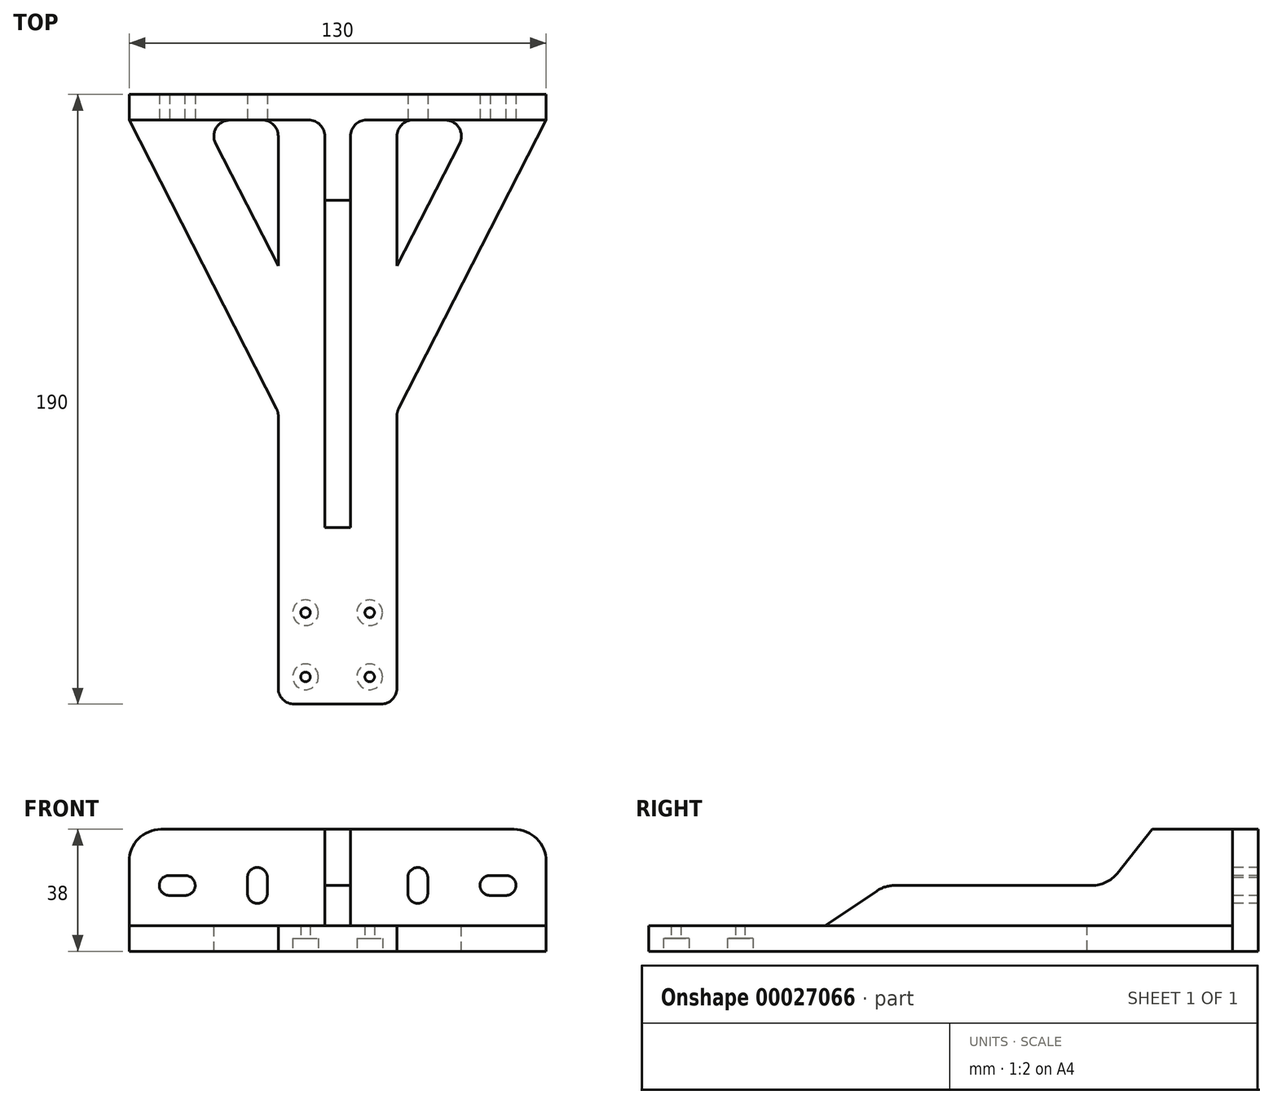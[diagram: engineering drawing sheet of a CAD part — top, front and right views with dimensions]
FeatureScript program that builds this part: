
annotation { "Feature Type Name" : "Feature", "Feature Type Description" : "" }
export const myFeature = defineFeature(function(context is Context, id is Id, definition is map)
    precondition{}
    {
        {
            var Q0;
            Q0=qCreatedBy(makeId("Top.planeOp"),FACE);
            var sketch = newSketch(context, id + "F0", { "sketchPlane" : qUnion([Q0])});
            skLineSegment(sketch, "E0", {"start": v(21.29, 30.4) * mm, "end": v(21.29, -54.4) * mm});
            skLineSegment(sketch, "E1", {"start": v(16.29, -59.4) * mm, "end": v(-10.71, -59.4) * mm});
            skLineSegment(sketch, "E2", {"start": v(-15.71, -54.4) * mm, "end": v(-15.71, 30.4) * mm});
            skLineSegment(sketch, "E3", {"start": v(-62.21, 130.6) * mm, "end": v(67.79, 130.6) * mm});
            skLineSegment(sketch, "E4", {"start": v(67.79, 130.6) * mm, "end": v(67.79, 122.6) * mm});
            skLineSegment(sketch, "E5", {"start": v(-62.21, 122.6) * mm, "end": v(-62.21, 130.6) * mm});
            skLineSegment(sketch, "E6", {"start": v(-16.26, 32.67) * mm, "end": v(-62.21, 122.6) * mm});
            skLineSegment(sketch, "E7", {"start": v(21.83, 32.67) * mm, "end": v(67.79, 122.6) * mm});
            skPoint(sketch, "E8.end.orphan", {"position": v(21.29, 122.6) * mm});
            skPoint(sketch, "E9.orphan", {"position": v(-15.71, 122.6) * mm});
            skPoint(sketch, "E10.visualSharp", {"position": v(-15.71, -59.4) * mm});
            skArc(sketch, "E10.filletArc", {"start": v(-15.71, -54.4) * mm, "mid": v(-14.25, -57.93) * mm, "end": v(-10.71, -59.4) * mm});
            skPoint(sketch, "E11.visualSharp", {"position": v(21.29, -59.4) * mm});
            skArc(sketch, "E11.filletArc", {"start": v(16.29, -59.4) * mm, "mid": v(19.82, -57.93) * mm, "end": v(21.29, -54.4) * mm});
            skPoint(sketch, "E12.visualSharp", {"position": v(21.29, 31.6) * mm});
            skArc(sketch, "E12.filletArc", {"start": v(21.83, 32.67) * mm, "mid": v(21.42, 31.57) * mm, "end": v(21.29, 30.4) * mm});
            skPoint(sketch, "E13.visualSharp", {"position": v(-15.71, 31.6) * mm});
            skArc(sketch, "E13.filletArc", {"start": v(-15.71, 30.4) * mm, "mid": v(-15.85, 31.57) * mm, "end": v(-16.26, 32.67) * mm});
            skLineSegment(sketch, "E14", {"start": v(-15.71, 122.6) * mm, "end": v(-38.96, 122.6) * mm});
            skLineSegment(sketch, "E15", {"start": v(-15.71, 122.6) * mm, "end": v(-15.71, 77.1) * mm});
            skLineSegment(sketch, "E16", {"start": v(-38.96, 122.6) * mm, "end": v(-15.71, 77.1) * mm});
            skLineSegment(sketch, "E17.MirrorCS", {"start": v(21.29, 122.6) * mm, "end": v(21.29, 77.1) * mm});
            skLineSegment(sketch, "E18.MirrorCS", {"start": v(44.54, 122.6) * mm, "end": v(21.29, 77.1) * mm});
            skLineSegment(sketch, "E19.MirrorCS", {"start": v(21.29, 122.6) * mm, "end": v(44.54, 122.6) * mm});
            skSolve(sketch);
        }
        {
            var Q0;
            Q0=makeQuery(id+"F0.imprint","IMPRINT",FACE,{"disambiguationData":[TD([[makeQuery(id+"F0.imprint","IMPRINT",EDGE,{"derivedFrom":sQuery(id+"F0.wireOp",EDGE,"E0")}),-1.0]])]});
            extrude(context, id + "F1", {"entities" : qUnion([Q0]), "depth" : 8 * mm});
        }
        {
            var Q0;
            Q0=makeQuery(id+"F1.opExtrude","CAP_FACE",FACE,{"disambiguationData":[OSD([sQuery(id+"F0.wireOp",EDGE,"E0"),sQuery(id+"F0.wireOp",EDGE,"E1"),sQuery(id+"F0.wireOp",EDGE,"E2"),sQuery(id+"F0.wireOp",EDGE,"E3"),sQuery(id+"F0.wireOp",EDGE,"E4"),sQuery(id+"F0.wireOp",EDGE,"E5"),sQuery(id+"F0.wireOp",EDGE,"E6"),sQuery(id+"F0.wireOp",EDGE,"E7"),sQuery(id+"F0.wireOp",EDGE,"E10.filletArc"),sQuery(id+"F0.wireOp",EDGE,"E11.filletArc"),sQuery(id+"F0.wireOp",EDGE,"E12.filletArc"),sQuery(id+"F0.wireOp",EDGE,"E13.filletArc"),sQuery(id+"F0.wireOp",EDGE,"E14"),sQuery(id+"F0.wireOp",EDGE,"E15"),sQuery(id+"F0.wireOp",EDGE,"E16"),sQuery(id+"F0.wireOp",EDGE,"E17.MirrorCS"),sQuery(id+"F0.wireOp",EDGE,"E18.MirrorCS"),sQuery(id+"F0.wireOp",EDGE,"E19.MirrorCS")])],"isStart":false});
            var sketch = newSketch(context, id + "F2", { "sketchPlane" : qUnion([Q0])});
            skLineSegment(sketch, "E20.bottom", {"start": v(-62.21, 122.6) * mm, "end": v(-1.21, 122.6) * mm});
            skLineSegment(sketch, "E20.top", {"start": v(-62.21, 130.6) * mm, "end": v(67.79, 130.6) * mm});
            skLineSegment(sketch, "E20.left", {"start": v(-62.21, 122.6) * mm, "end": v(-62.21, 130.6) * mm});
            skLineSegment(sketch, "E20.right", {"start": v(67.79, 122.6) * mm, "end": v(67.79, 130.6) * mm});
            skLineSegment(sketch, "E21.top", {"start": v(-1.21, -4.4) * mm, "end": v(6.79, -4.4) * mm});
            skLineSegment(sketch, "E21.left", {"start": v(-1.21, 122.6) * mm, "end": v(-1.21, -4.4) * mm});
            skLineSegment(sketch, "E21.right", {"start": v(6.79, 122.6) * mm, "end": v(6.79, -4.4) * mm});
            skLineSegment(sketch, "E22.trimOffspring", {"start": v(6.79, 122.6) * mm, "end": v(67.79, 122.6) * mm});
            skSolve(sketch);
        }
        {
            var Q0;
            Q0 = qSketchRegion(id + "F2", true);
            extrude(context, id + "F3", {"entities" : qUnion([Q0]), "operationType" : NewBodyOperationType.ADD, "depth" : 30 * mm});
        }
        {
            var Q0;
            Q0=makeQuery(id+"F3.opExtrude","SWEPT_FACE",FACE,{"disambiguationData":[OSD([sQuery(id+"F2.wireOp",EDGE,"E21.right")])]});
            var sketch = newSketch(context, id + "F4", { "sketchPlane" : qUnion([Q0])});
            skLineSegment(sketch, "E23", {"start": v(97.6, 38) * mm, "end": v(83.6, 20.5) * mm});
            skLineSegment(sketch, "E24", {"start": v(83.6, 20.5) * mm, "end": v(14.2, 20.5) * mm});
            skLineSegment(sketch, "E25", {"start": v(14.2, 20.5) * mm, "end": v(-4.4, 8) * mm});
            skLineSegment(sketch, "E26", {"start": v(-4.4, 8) * mm, "end": v(-4.62, 38.23) * mm});
            skLineSegment(sketch, "E27", {"start": v(-4.62, 38.23) * mm, "end": v(97.6, 38) * mm});
            skSolve(sketch);
        }
        {
            var Q0;
            Q0 = qSketchRegion(id + "F4", true);
            extrude(context, id + "F5", {"entities" : qUnion([Q0]), "operationType" : NewBodyOperationType.REMOVE, "endBound" : BoundingType.THROUGH_ALL, "oppositeDirection" : true, "depth" : 25 * mm});
        }
        {
            var Q0;
            Q0=makeQuery(id+"F5.boolean.opBoolean","COPY",EDGE,{"derivedFrom":makeQuery(id+"F5.opExtrude","SWEPT_EDGE",EDGE,{"disambiguationData":[OSD([sQuery(id+"F2.wireOp",EDGE,"E21.right"),sQuery(id+"F4.wireOp",EDGE,"E23"),sQuery(id+"F4.wireOp",EDGE,"E27")])]})});
            var Q1;
            Q1=makeQuery(id+"F5.boolean.opBoolean","COPY",EDGE,{"derivedFrom":makeQuery(id+"F5.opExtrude","SWEPT_EDGE",EDGE,{"disambiguationData":[OSD([sQuery(id+"F4.wireOp",EDGE,"E23"),sQuery(id+"F4.wireOp",EDGE,"E24")])]})});
            var Q2;
            Q2=makeQuery(id+"F5.boolean.opBoolean","COPY",EDGE,{"derivedFrom":makeQuery(id+"F5.opExtrude","SWEPT_EDGE",EDGE,{"disambiguationData":[OSD([sQuery(id+"F4.wireOp",EDGE,"E24"),sQuery(id+"F4.wireOp",EDGE,"E25")])]})});
            var Q3;
            Q3=makeQuery(id+"F3.opExtrude","CAP_EDGE",EDGE,{"disambiguationData":[OSD([sQuery(id+"F2.wireOp",EDGE,"E20.left")])],"isStart":false});
            var Q4;
            Q4=makeQuery(id+"F3.opExtrude","CAP_EDGE",EDGE,{"disambiguationData":[OSD([sQuery(id+"F2.wireOp",EDGE,"E20.right")])],"isStart":false});
            fillet(context, id + "F6", {"entities" : qUnion([Q0, Q1, Q2, Q3, Q4]), "radius" : 10 * mm, "tangentPropagation" : true, "allowEdgeOverflow" : false});
        }
        {
            var Q0;
            Q0=makeQuery(id+"F1.opExtrude","CAP_FACE",FACE,{"disambiguationData":[OSD([sQuery(id+"F0.wireOp",EDGE,"E0"),sQuery(id+"F0.wireOp",EDGE,"E1"),sQuery(id+"F0.wireOp",EDGE,"E2"),sQuery(id+"F0.wireOp",EDGE,"E3"),sQuery(id+"F0.wireOp",EDGE,"E4"),sQuery(id+"F0.wireOp",EDGE,"E5"),sQuery(id+"F0.wireOp",EDGE,"E6"),sQuery(id+"F0.wireOp",EDGE,"E7"),sQuery(id+"F0.wireOp",EDGE,"E10.filletArc"),sQuery(id+"F0.wireOp",EDGE,"E11.filletArc"),sQuery(id+"F0.wireOp",EDGE,"E12.filletArc"),sQuery(id+"F0.wireOp",EDGE,"E13.filletArc"),sQuery(id+"F0.wireOp",EDGE,"E14"),sQuery(id+"F0.wireOp",EDGE,"E15"),sQuery(id+"F0.wireOp",EDGE,"E16"),sQuery(id+"F0.wireOp",EDGE,"E17.MirrorCS"),sQuery(id+"F0.wireOp",EDGE,"E18.MirrorCS"),sQuery(id+"F0.wireOp",EDGE,"E19.MirrorCS")])],"isStart":true});
            var sketch = newSketch(context, id + "F7", { "sketchPlane" : qUnion([Q0])});
            skLineSegment(sketch, "E28.rect.bottom", {"start": v(-7.21, 30.9) * mm, "end": v(12.79, 30.9) * mm});
            skLineSegment(sketch, "E28.rect.top", {"start": v(-7.21, 50.9) * mm, "end": v(12.79, 50.9) * mm});
            skLineSegment(sketch, "E28.rect.left", {"start": v(-7.21, 30.9) * mm, "end": v(-7.21, 50.9) * mm});
            skLineSegment(sketch, "E28.rect.right", {"start": v(12.79, 30.9) * mm, "end": v(12.79, 50.9) * mm});
            skPoint(sketch, "E28.rect.middle", {"position": v(2.79, 40.9) * mm});
            skLineSegment(sketch, "E29", {"start": v(2.79, 59.4) * mm, "end": v(2.79, 50.9) * mm, "construction": true});
            skSolve(sketch);
        }
        {
            var Q0;
            Q0=sQuery(id+"F7.wireOp",VERTEX,"E28.rect.right.end");
            var Q1;
            Q1=sQuery(id+"F7.wireOp",VERTEX,"E28.rect.bottom.start");
            var Q2;
            Q2=sQuery(id+"F7.wireOp",VERTEX,"E28.rect.left.end");
            var Q3;
            Q3=sQuery(id+"F7.wireOp",VERTEX,"E28.rect.bottom.end");
            var Q4;
            Q4=makeQuery(id+"F1.opExtrude","SWEPT_BODY",BODY,{"disambiguationData":[OSD([sQuery(id+"F0.wireOp",EDGE,"E0"),sQuery(id+"F0.wireOp",EDGE,"E1"),sQuery(id+"F0.wireOp",EDGE,"E2"),sQuery(id+"F0.wireOp",EDGE,"E3"),sQuery(id+"F0.wireOp",EDGE,"E4"),sQuery(id+"F0.wireOp",EDGE,"E5"),sQuery(id+"F0.wireOp",EDGE,"E6"),sQuery(id+"F0.wireOp",EDGE,"E7"),sQuery(id+"F0.wireOp",EDGE,"E10.filletArc"),sQuery(id+"F0.wireOp",EDGE,"E11.filletArc"),sQuery(id+"F0.wireOp",EDGE,"E12.filletArc"),sQuery(id+"F0.wireOp",EDGE,"E13.filletArc"),sQuery(id+"F0.wireOp",EDGE,"E14"),sQuery(id+"F0.wireOp",EDGE,"E15"),sQuery(id+"F0.wireOp",EDGE,"E16"),sQuery(id+"F0.wireOp",EDGE,"E17.MirrorCS"),sQuery(id+"F0.wireOp",EDGE,"E18.MirrorCS"),sQuery(id+"F0.wireOp",EDGE,"E19.MirrorCS")])]});
            hole(context, id + "F8", {"style" : HoleStyle.C_BORE, "holeDiameter" : 3 * mm, "cBoreDiameter" : 8 * mm, "cBoreDepth" : 4 * mm, "endStyle" : HoleEndStyle.THROUGH, "locations" : qUnion([Q0, Q1, Q2, Q3]), "scope" : qUnion([Q4])});
        }
        {
            var Q0;
            Q0=makeQuery(id+"F3.boolean.opBoolean","MERGE",FACE,{"derivedFrom":[makeQuery(id+"F1.opExtrude","SWEPT_FACE",FACE,{"disambiguationData":[OSD([sQuery(id+"F0.wireOp",EDGE,"E19.MirrorCS")])]}),makeQuery(id+"F3.opExtrude","SWEPT_FACE",FACE,{"disambiguationData":[OSD([sQuery(id+"F2.wireOp",EDGE,"E22.trimOffspring")])]})]});
            var sketch = newSketch(context, id + "F9", { "sketchPlane" : qUnion([Q0])});
            skLineSegment(sketch, "E30", {"start": v(52.79, 20.5) * mm, "end": v(-47.21, 20.5) * mm, "construction": true});
            skLineSegment(sketch, "E31", {"start": v(52.79, 20.5) * mm, "end": v(27.79, 20.5) * mm, "construction": true});
            skLineSegment(sketch, "E32", {"start": v(27.79, 18) * mm, "end": v(27.79, 23) * mm});
            skLineSegment(sketch, "E33", {"start": v(55.29, 20.5) * mm, "end": v(50.29, 20.5) * mm, "construction": true});
            skLineSegment(sketch, "E34", {"start": v(2.79, 8) * mm, "end": v(2.79, 20.5) * mm, "construction": true});
            skLineSegment(sketch, "E35.MirrorCS", {"start": v(-47.21, 20.5) * mm, "end": v(-22.21, 20.5) * mm, "construction": true});
            skLineSegment(sketch, "E36.MirrorCS", {"start": v(-49.71, 20.5) * mm, "end": v(-44.71, 20.5) * mm, "construction": true});
            skArc(sketch, "E37", {"start": v(-49.6, 23.6) * mm, "mid": v(-52.81, 20.56) * mm, "end": v(-49.71, 17.4) * mm});
            skArc(sketch, "E38", {"start": v(-44.72, 17.4) * mm, "mid": v(-41.61, 20.56) * mm, "end": v(-44.84, 23.6) * mm});
            skLineSegment(sketch, "E39", {"start": v(-49.84, 23.6) * mm, "end": v(-44.84, 23.6) * mm});
            skLineSegment(sketch, "E40", {"start": v(-44.72, 17.4) * mm, "end": v(-49.71, 17.4) * mm});
            skArc(sketch, "E41.MirrorCS", {"start": v(50.3, 17.4) * mm, "mid": v(47.19, 20.56) * mm, "end": v(50.4, 23.6) * mm});
            skLineSegment(sketch, "E42.MirrorCS", {"start": v(55.4, 23.6) * mm, "end": v(50.4, 23.6) * mm});
            skArc(sketch, "E43.MirrorCS", {"start": v(55.16, 23.6) * mm, "mid": v(58.39, 20.56) * mm, "end": v(55.29, 17.4) * mm});
            skLineSegment(sketch, "E44.MirrorCS", {"start": v(50.3, 17.4) * mm, "end": v(55.29, 17.4) * mm});
            skArc(sketch, "E45", {"start": v(-19.12, 22.88) * mm, "mid": v(-22.17, 26.1) * mm, "end": v(-25.31, 22.97) * mm});
            skArc(sketch, "E46", {"start": v(-25.31, 18) * mm, "mid": v(-22.21, 14.9) * mm, "end": v(-19.11, 18) * mm});
            skLineSegment(sketch, "E47", {"start": v(-19.12, 22.88) * mm, "end": v(-19.11, 18) * mm});
            skLineSegment(sketch, "E48", {"start": v(-25.31, 22.97) * mm, "end": v(-25.31, 18) * mm});
            skArc(sketch, "E49.MirrorCS", {"start": v(24.69, 22.88) * mm, "mid": v(27.74, 26.1) * mm, "end": v(30.89, 22.97) * mm});
            skLineSegment(sketch, "E50.MirrorCS", {"start": v(24.69, 22.88) * mm, "end": v(24.69, 18) * mm});
            skArc(sketch, "E51.MirrorCS", {"start": v(30.89, 18) * mm, "mid": v(27.79, 14.9) * mm, "end": v(24.69, 18) * mm});
            skLineSegment(sketch, "E52.MirrorCS", {"start": v(30.89, 22.97) * mm, "end": v(30.89, 18) * mm});
            skArc(sketch, "E53.MirrorCS", {"start": v(24.69, 22.88) * mm, "mid": v(27.74, 26.1) * mm, "end": v(30.89, 22.97) * mm, "construction": true});
            skSolve(sketch);
        }
        {
            var Q0;
            Q0 = qSketchRegion(id + "F9", true);
            extrude(context, id + "F10", {"entities" : qUnion([Q0]), "operationType" : NewBodyOperationType.REMOVE, "endBound" : BoundingType.THROUGH_ALL, "oppositeDirection" : true, "depth" : 25 * mm});
        }
        {
            var Q0;
            Q0=makeQuery(id+"F3.opExtrude","SWEPT_EDGE",EDGE,{"disambiguationData":[OSD([sQuery(id+"F2.wireOp",EDGE,"E20.bottom"),sQuery(id+"F2.wireOp",EDGE,"E21.left")])]});
            var Q1;
            Q1=makeQuery(id+"F3.opExtrude","SWEPT_EDGE",EDGE,{"disambiguationData":[OSD([sQuery(id+"F2.wireOp",EDGE,"E21.right"),sQuery(id+"F2.wireOp",EDGE,"E22.trimOffspring")])]});
            var Q2;
            Q2=makeQuery(id+"F1.opExtrude","SWEPT_EDGE",EDGE,{"disambiguationData":[OSD([sQuery(id+"F0.wireOp",EDGE,"E17.MirrorCS"),sQuery(id+"F0.wireOp",EDGE,"E19.MirrorCS")])]});
            var Q3;
            Q3=makeQuery(id+"F1.opExtrude","SWEPT_EDGE",EDGE,{"disambiguationData":[OSD([sQuery(id+"F0.wireOp",EDGE,"E18.MirrorCS"),sQuery(id+"F0.wireOp",EDGE,"E19.MirrorCS")])]});
            var Q4;
            Q4=makeQuery(id+"F1.opExtrude","SWEPT_EDGE",EDGE,{"disambiguationData":[OSD([sQuery(id+"F0.wireOp",EDGE,"E14"),sQuery(id+"F0.wireOp",EDGE,"E15")])]});
            var Q5;
            Q5=makeQuery(id+"F1.opExtrude","SWEPT_EDGE",EDGE,{"disambiguationData":[OSD([sQuery(id+"F0.wireOp",EDGE,"E14"),sQuery(id+"F0.wireOp",EDGE,"E16")])]});
            fillet(context, id + "F11", {"entities" : qUnion([Q0, Q1, Q2, Q3, Q4, Q5]), "radius" : 5 * mm, "tangentPropagation" : true, "allowEdgeOverflow" : false});
        }
    });
